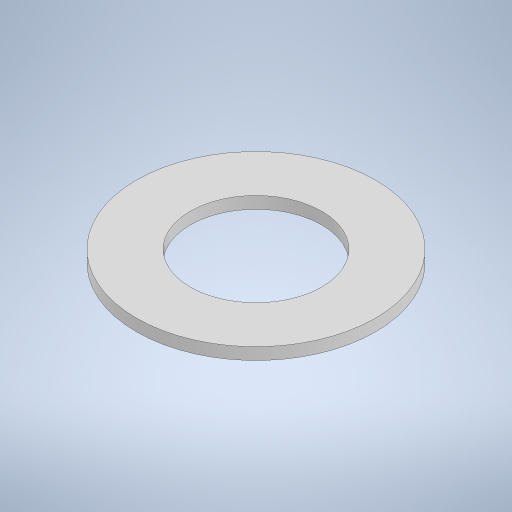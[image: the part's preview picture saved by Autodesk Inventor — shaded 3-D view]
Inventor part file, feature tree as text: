
AUTODESK INVENTOR PART (.ipt)
format: ipt  version: 2024.1 (Build 281209000, 209)  size: 227,840 bytes
history: native  units: mm
features: other x1, extrude x1, sketch x1
ambient origin geometry x8: Origin, YZ Plane, XZ Plane, XY Plane, X Axis, Y Axis, Z Axis, Center Point
bodies: Body1 (feature_tree)
feature tree (3):
  other  "ソリッド1"
  extrude  "押し出し1"  Depth=22.0mm
  sketch  "スケッチ1"
